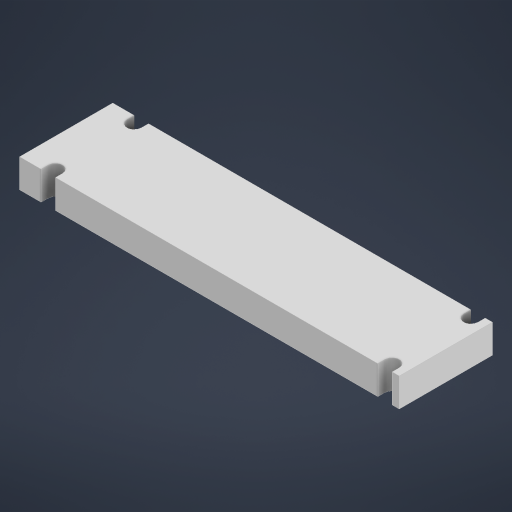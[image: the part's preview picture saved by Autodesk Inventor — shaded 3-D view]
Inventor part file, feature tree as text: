
AUTODESK INVENTOR PART (.ipt)
format: ipt  version: 2023.2 (Build 272271000, 271)  size: 223,744 bytes
history: native  units: mm
features: sketch x1
ambient origin geometry x8: Origin, YZ Plane, XZ Plane, XY Plane, X Axis, Y Axis, Z Axis, Center Point
bodies: Body1 (feature_tree)
feature tree (1):
  sketch  "Sketch1"  dims[d228=13.0mm d229=53.0mm d233=4.0mm d234=2.0mm d235=11.0mm d237=2.0mm d238=4.0mm d239=0.0mm d9=0.5mm d10=0.872665mm d11=0.5mm d12=0.872665mm d13=0.5mm d14=0.872665mm d27=0.5mm d28=0.872665mm d29=0.5mm d30=0.872665mm d88=0.5mm d89=0.872665mm d90=0.5mm d91=0.872665mm d116=0.5mm d117=0.872665mm d118=0.5mm d119=0.872665mm d154=0.5mm d155=0.872665mm d156=0.5mm d157=0.872665mm d181=0.5mm d182=0.872665mm d183=0.5mm d184=0.872665mm d221=0.5mm d222=0.872665mm d223=0.5mm d224=0.872665mm]
